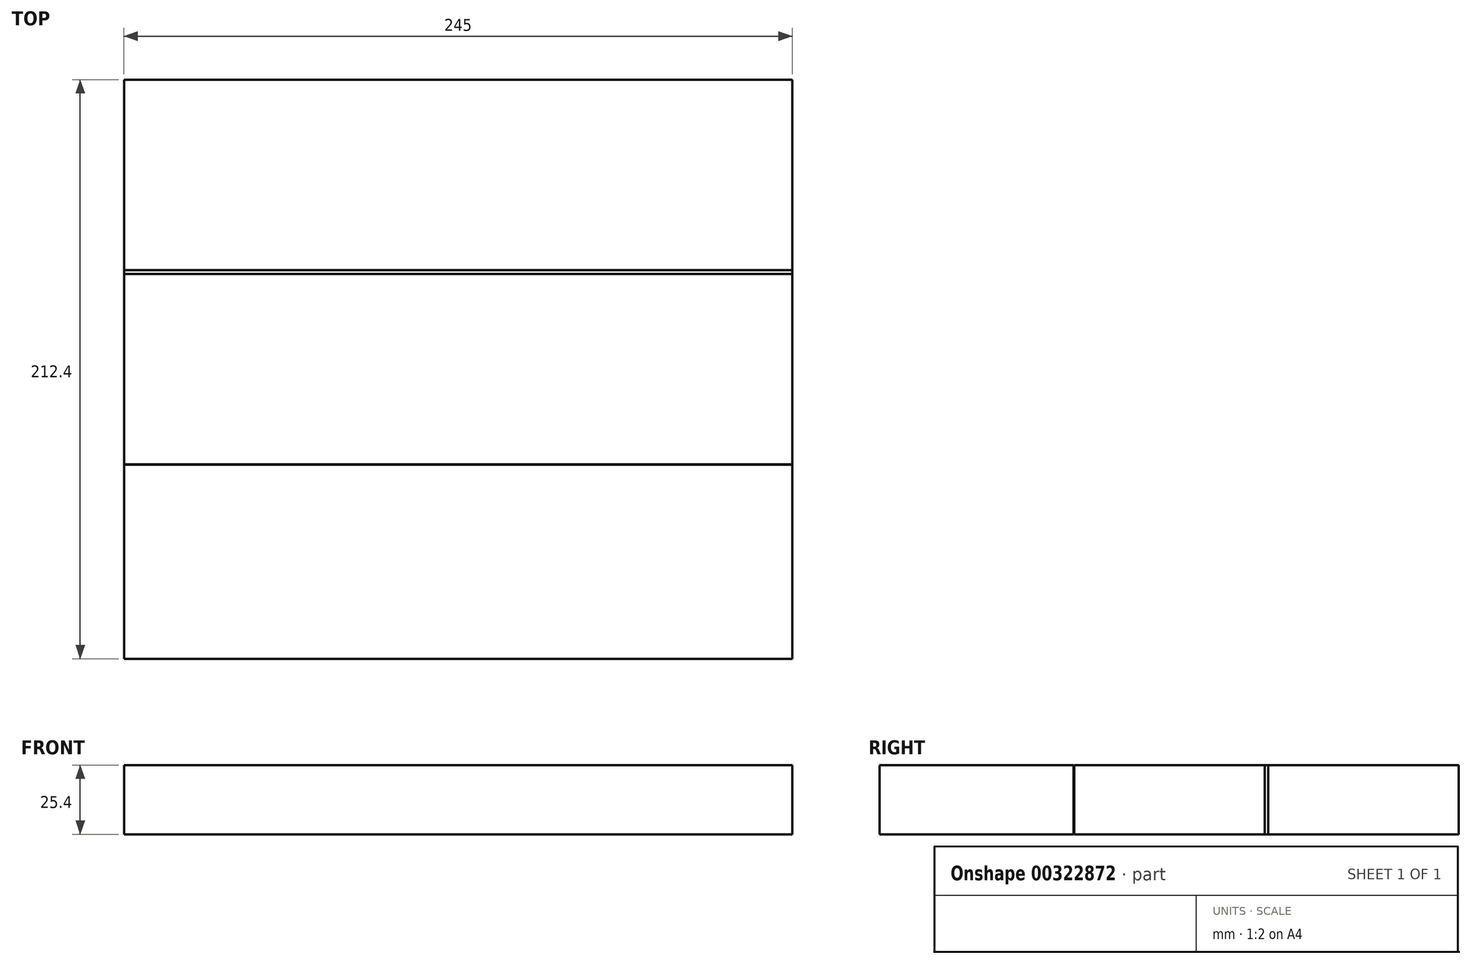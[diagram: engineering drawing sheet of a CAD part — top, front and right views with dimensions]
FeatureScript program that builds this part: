
annotation { "Feature Type Name" : "Feature", "Feature Type Description" : "" }
export const myFeature = defineFeature(function(context is Context, id is Id, definition is map)
    precondition{}
    {
        {
            var Q0;
            Q0=qCreatedBy(makeId("Top.planeOp"),FACE);
            var sketch = newSketch(context, id + "F0", { "sketchPlane" : qUnion([Q0])});
            skLineSegment(sketch, "E0.bottom", {"start": v(-137.76, 43.13) * mm, "end": v(107.24, 43.13) * mm});
            skLineSegment(sketch, "E0.top", {"start": v(-137.76, -28.04) * mm, "end": v(107.24, -28.04) * mm});
            skLineSegment(sketch, "E0.left", {"start": v(-137.76, 43.13) * mm, "end": v(-137.76, -28.04) * mm});
            skLineSegment(sketch, "E0.right", {"start": v(107.24, 43.13) * mm, "end": v(107.24, -28.04) * mm});
            skSolve(sketch);
        }
        {
            var Q0;
            Q0=makeQuery(id+"F0.imprint","IMPRINT",FACE,{"disambiguationData":[TD([[makeQuery(id+"F0.imprint","IMPRINT",EDGE,{"derivedFrom":sQuery(id+"F0.wireOp",EDGE,"E0.bottom")}),-1.0]])]});
            extrude(context, id + "F1", {"entities" : qUnion([Q0]), "depth" : 25.4 * mm});
        }
        {
            var Q0;
            Q0=makeQuery(id+"F1.opExtrude","SWEPT_BODY",BODY,{"disambiguationData":[OSD([sQuery(id+"F0.wireOp",EDGE,"E0.bottom"),sQuery(id+"F0.wireOp",EDGE,"E0.top"),sQuery(id+"F0.wireOp",EDGE,"E0.left"),sQuery(id+"F0.wireOp",EDGE,"E0.right")])]});
            transform(context, id + "F2", {"entities" : qUnion([Q0]), "transformType" : TransformType.TRANSLATION_3D, "dx" : 0 * mm, "dy" : -71.37 * mm, "dz" : 0 * mm, "makeCopy" : true});
        }
        {
            var Q0;
            Q0=makeQuery(id+"F1.opExtrude","SWEPT_BODY",BODY,{"disambiguationData":[OSD([sQuery(id+"F0.wireOp",EDGE,"E0.bottom"),sQuery(id+"F0.wireOp",EDGE,"E0.top"),sQuery(id+"F0.wireOp",EDGE,"E0.left"),sQuery(id+"F0.wireOp",EDGE,"E0.right")])]});
            transform(context, id + "F3", {"entities" : qUnion([Q0]), "transformType" : TransformType.TRANSLATION_3D, "dx" : 0 * mm, "dy" : 69.85 * mm, "dz" : 0 * mm, "makeCopy" : true});
        }
    });
